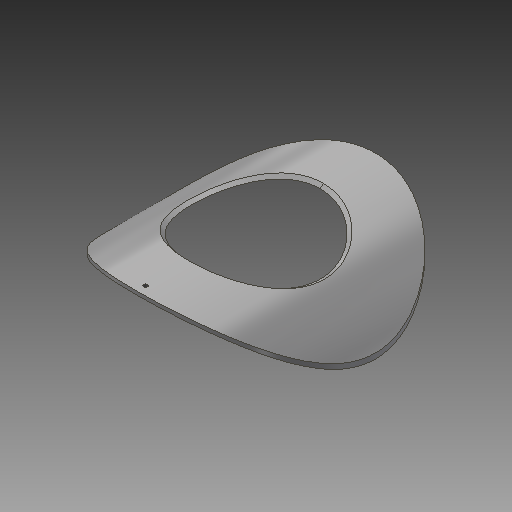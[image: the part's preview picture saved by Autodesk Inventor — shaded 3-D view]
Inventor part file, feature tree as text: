
AUTODESK INVENTOR PART (.ipt)
format: ipt  version: 2017.3 (Build 213257000, 257)  size: 207,360 bytes
history: native  units: in
note: dims shown in document units (in); Inventor stores cm internally (conversion verified against a paired STEP export)
features: sketch x5, extrude x2, sweep x1, plane x1, hole x1
ambient origin geometry x8: Origin, YZ Plane, XZ Plane, XY Plane, X Axis, Y Axis, Z Axis, Center Point
bodies: Solid1 (feature_tree)
feature tree (10):
  extrude  "Extrusion1"  Depth=34.75in
  extrude  "Extrusion2"  Depth=14.001in
  sketch  "Sketch3"  dims[d5=26.001in d6=26.0in d7=0.0in]
  sweep  "Sweep1"
  plane  "Work Plane1"
  hole  "Hole1"  [1 undecoded]
  sketch  "Sketch1"  dims[d0=34.0in d1=34.75in]
  sketch  "Sketch2"  dims[d2=26.001in d3=0.0in d4=14.001in]
  sketch  "3D Sketch1"
  sketch  "Sketch4"  dims[d9=0.25in d10=0.25in d11=0.2749in d12=0.5in d13=0.0in d14=0.0in d15=0.0625in d16=0.2979in d17=12.0005in d18=0.422in d19=0.395in d20=0.0246in d21=0.423in d22=0.375in d23=0.25in d24=0.5635in d25=1.0in d26=0.8108in]
note: 1 required parameter value undecoded (feature->parameter linkage not recoverable at this tier; creation-order binding heuristic only, values carry confidence <= 0.55)
